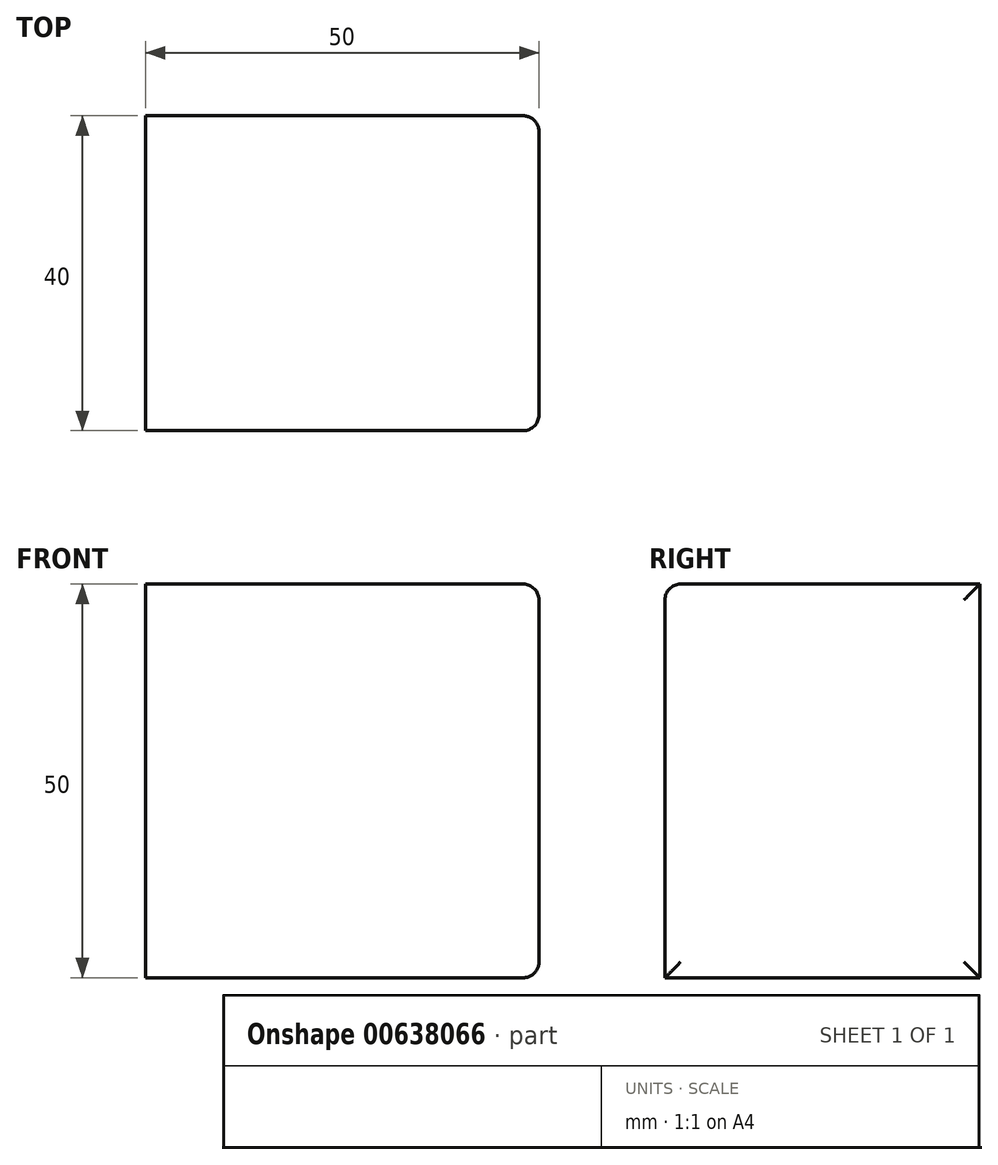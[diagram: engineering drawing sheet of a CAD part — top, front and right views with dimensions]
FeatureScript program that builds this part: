
annotation { "Feature Type Name" : "Feature", "Feature Type Description" : "" }
export const myFeature = defineFeature(function(context is Context, id is Id, definition is map)
    precondition{}
    {
        {
            var Q0;
            Q0=qCreatedBy(makeId("Top.planeOp"),FACE);
            var sketch = newSketch(context, id + "F0", { "sketchPlane" : qUnion([Q0])});
            skLineSegment(sketch, "E0.bottom", {"start": v(1.86, 0) * mm, "end": v(51.86, 0) * mm});
            skLineSegment(sketch, "E0.top", {"start": v(1.86, -40) * mm, "end": v(51.86, -40) * mm});
            skLineSegment(sketch, "E0.left", {"start": v(1.86, 0) * mm, "end": v(1.86, -40) * mm});
            skLineSegment(sketch, "E0.right", {"start": v(51.86, 0) * mm, "end": v(51.86, -40) * mm});
            skSolve(sketch);
        }
        {
            var Q0;
            Q0=makeQuery(id+"F0.imprint","IMPRINT",FACE,{"disambiguationData":[TD([[makeQuery(id+"F0.imprint","IMPRINT",EDGE,{"derivedFrom":sQuery(id+"F0.wireOp",EDGE,"E0.bottom")}),-1.0]])]});
            extrude(context, id + "F1", {"entities" : qUnion([Q0]), "depth" : 50 * mm, "offsetDistance" : 25 * mm});
        }
        {
            var Q0;
            Q0=makeQuery(id+"F1.opExtrude","CAP_EDGE",EDGE,{"disambiguationData":[OSD([sQuery(id+"F0.wireOp",EDGE,"E0.top")])],"isStart":false});
            var Q1;
            Q1=makeQuery(id+"F1.opExtrude","SWEPT_EDGE",EDGE,{"disambiguationData":[OSD([sQuery(id+"F0.wireOp",EDGE,"E0.top"),sQuery(id+"F0.wireOp",EDGE,"E0.right")])]});
            var Q2;
            Q2=makeQuery(id+"F1.opExtrude","SWEPT_FACE",FACE,{"disambiguationData":[OSD([sQuery(id+"F0.wireOp",EDGE,"E0.right")])]});
            fillet(context, id + "F2", {"entities" : qUnion([Q0, Q1, Q2]), "radius" : 2 * mm, "tangentPropagation" : true, "allowEdgeOverflow" : false});
        }
    });
